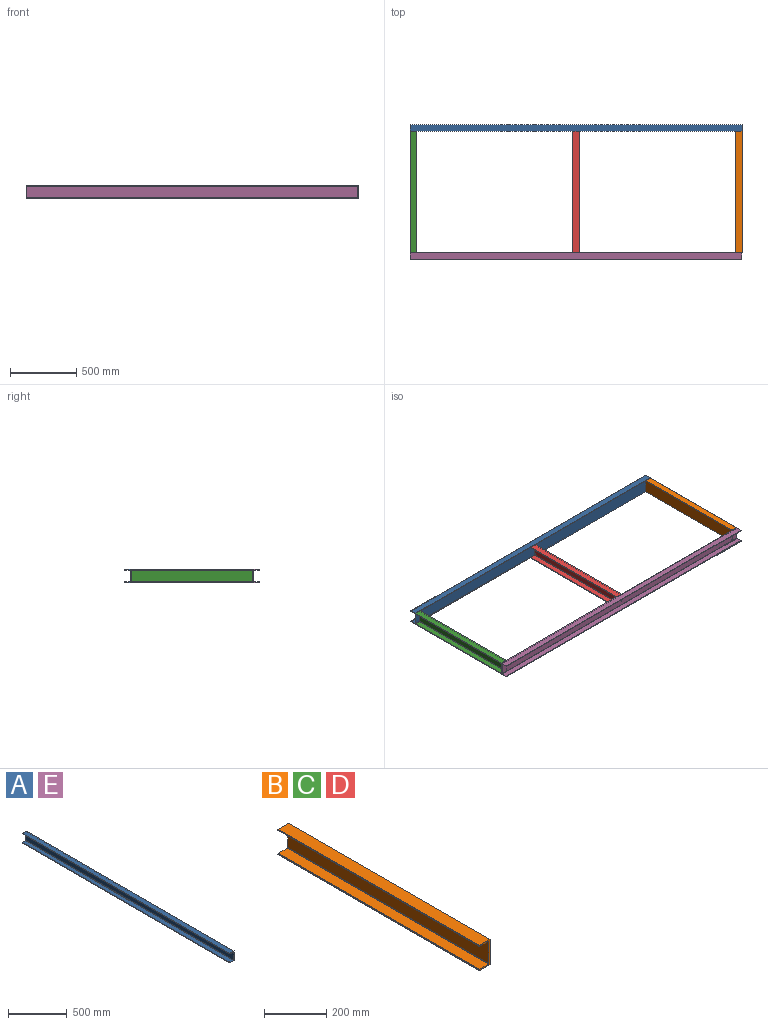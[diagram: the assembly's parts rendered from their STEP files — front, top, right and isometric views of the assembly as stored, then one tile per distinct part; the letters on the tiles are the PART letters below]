
ASSEMBLY  parts=5 mates=4
PART A: 14 faces, bbox 50x2500x100 mm
  f0: plane 2500x100mm, normal (1,0,0), area 250000mm2, adj f1,f11,f12,f13
  f1: plane 2500x50mm, normal (0,0,1), area 125000mm2, adj f0,f2,f12,f13
  f2: plane 2500x3mm, normal (-1,0,0), area 7500mm2, adj f1,f3,f12,f13
  f3: cylinder r=2mm len=2500mm, axis (0,1,0), area 7854mm2, adj f2,f4,f12,f13
  f4: plane 2500x41mm, normal (0,0,-1), area 102500mm2, adj f3,f5,f12,f13
  f5: cylinder r=2mm len=2500mm, axis (0,1,0), area 7854mm2, adj f4,f6,f12,f13
  f6: plane 2500x86mm, normal (-1,0,0), area 215000mm2, adj f5,f7,f12,f13
  f7: cylinder r=2mm len=2500mm, axis (0,1,0), area 7854mm2, adj f6,f8,f12,f13
  f8: plane 2500x41mm, normal (0,0,1), area 102500mm2, adj f7,f9,f12,f13
  f9: cylinder r=2mm len=2500mm, axis (0,1,0), area 7854mm2, adj f8,f10,f12,f13
  f10: plane 2500x3mm, normal (-1,0,0), area 7500mm2, adj f9,f11,f12,f13
  f11: plane 2500x50mm, normal (0,0,-1), area 125000mm2, adj f0,f10,f12,f13
  f12: plane 100x50mm, normal (0,-1,0), area 950mm2, adj f0,f1,f2,f3,f4,f5,f6,f7
  f13: plane 100x50mm, normal (0,1,0), area 950mm2, adj f0,f1,f2,f3,f4,f5,f6,f7
PART B: 14 faces, bbox 50x916x100 mm
  f0: plane 916x100mm, normal (1,0,0), area 91600mm2, adj f1,f11,f12,f13
  f1: plane 916x50mm, normal (0,0,1), area 45800mm2, adj f0,f2,f12,f13
  f2: plane 916x3mm, normal (-1,0,0), area 2748mm2, adj f1,f3,f12,f13
  f3: cylinder r=2mm len=916mm, axis (0,1,0), area 2877.7mm2, adj f2,f4,f12,f13
  f4: plane 916x41mm, normal (0,0,-1), area 37556mm2, adj f3,f5,f12,f13
  f5: cylinder r=2mm len=916mm, axis (0,1,0), area 2877.7mm2, adj f4,f6,f12,f13
  f6: plane 916x86mm, normal (-1,0,0), area 78776mm2, adj f5,f7,f12,f13
  f7: cylinder r=2mm len=916mm, axis (0,1,0), area 2877.7mm2, adj f6,f8,f12,f13
  f8: plane 916x41mm, normal (0,0,1), area 37556mm2, adj f7,f9,f12,f13
  f9: cylinder r=2mm len=916mm, axis (0,1,0), area 2877.7mm2, adj f8,f10,f12,f13
  f10: plane 916x3mm, normal (-1,0,0), area 2748mm2, adj f9,f11,f12,f13
  f11: plane 916x50mm, normal (0,0,-1), area 45800mm2, adj f0,f10,f12,f13
  f12: plane 100x50mm, normal (0,-1,0), area 950mm2, adj f0,f1,f2,f3,f4,f5,f6,f7
  f13: plane 100x50mm, normal (0,1,0), area 950mm2, adj f0,f1,f2,f3,f4,f5,f6,f7
PART C: same geometry as B
PART D: same geometry as B
PART E: same geometry as A
PLACE A rot(axis=(0,0,-1),90deg) t=(197.05,32.44,-490.92)mm
PLACE B rot(axis=(0,0,1),180deg) t=(147.05,-883.56,-490.92)mm
PLACE C t=(-2252.95,32.44,-490.92)mm
PLACE D t=(-1027.95,32.44,-490.92)mm
PLACE E rot(axis=(0,0,1),90deg) t=(-2302.95,-883.56,-490.92)mm
MATE fastened A.f1 <-> B.f1  axis (0,0,1) through (197.05,32.44,-390.92)mm
MATE fastened C.f1 <-> E.f1  axis (0,0,1) through (-2302.95,-883.56,-390.92)mm
MATE fastened D.f1 <-> E.f1  axis (0,0,1) through (-1052.95,-883.56,-390.92)mm
MATE fastened B.f1 <-> E.f1  axis (0,0,1) through (197.05,-883.56,-390.92)mm
